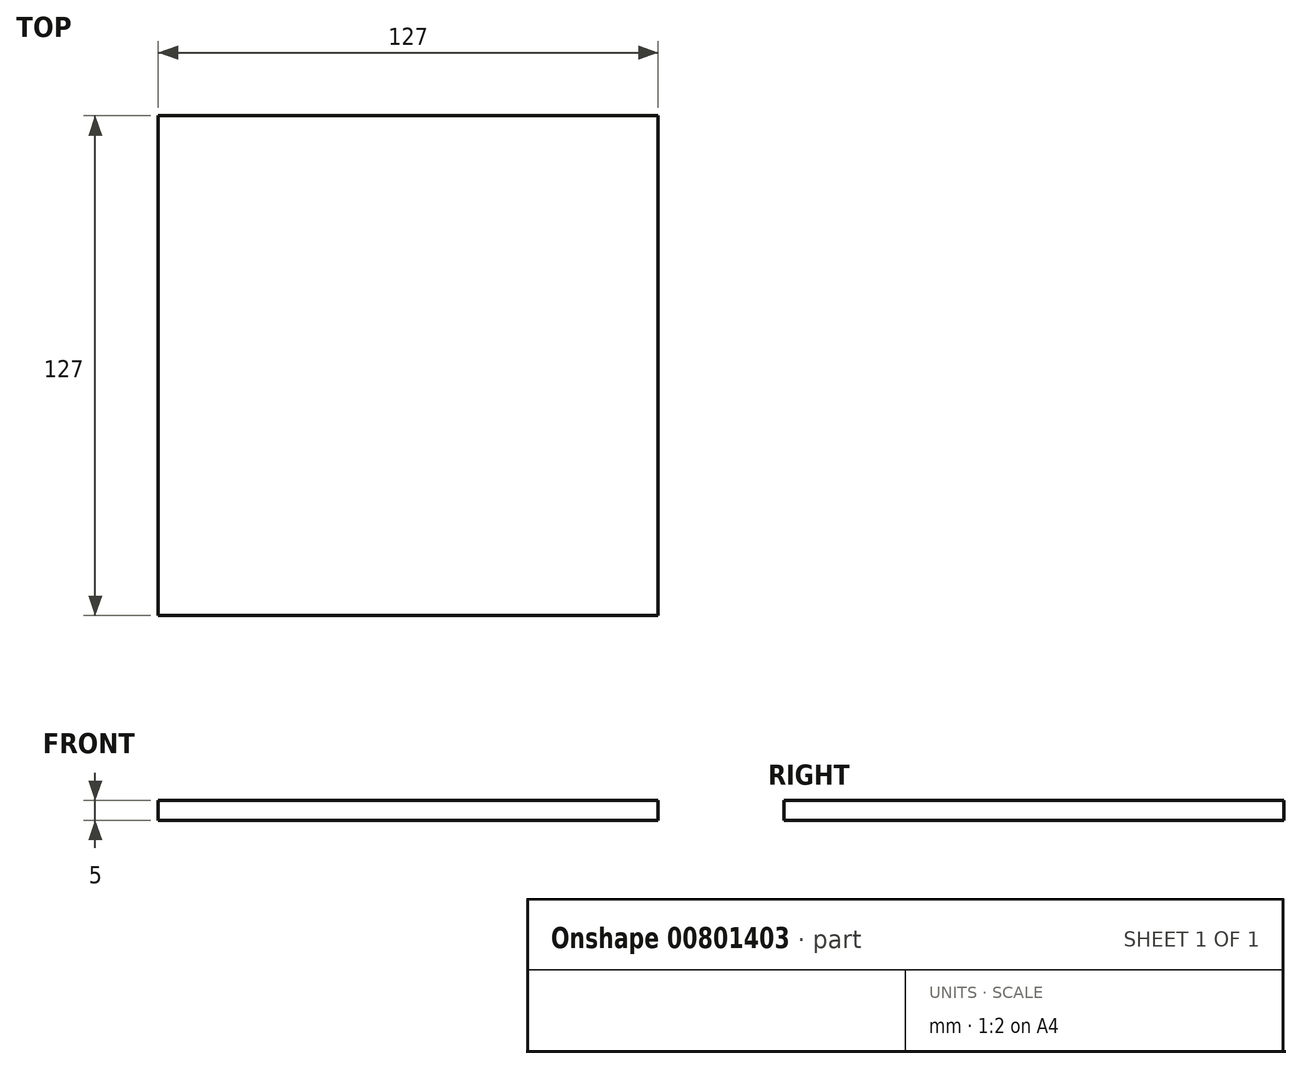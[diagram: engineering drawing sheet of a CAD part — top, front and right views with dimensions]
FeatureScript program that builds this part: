
annotation { "Feature Type Name" : "Feature", "Feature Type Description" : "" }
export const myFeature = defineFeature(function(context is Context, id is Id, definition is map)
    precondition{}
    {
        {
            var Q0;
            Q0=qCreatedBy(makeId("Top.planeOp"),FACE);
            var sketch = newSketch(context, id + "F0", { "sketchPlane" : qUnion([Q0])});
            skLineSegment(sketch, "E0.bottom", {"start": v(-63.5, 63.5) * mm, "end": v(63.5, 63.5) * mm});
            skLineSegment(sketch, "E0.top", {"start": v(-63.5, -63.5) * mm, "end": v(63.5, -63.5) * mm});
            skLineSegment(sketch, "E0.left", {"start": v(-63.5, 63.5) * mm, "end": v(-63.5, -63.5) * mm});
            skLineSegment(sketch, "E0.right", {"start": v(63.5, 63.5) * mm, "end": v(63.5, -63.5) * mm});
            skPoint(sketch, "E0.middle", {"position": v(0, 0) * mm});
            skSolve(sketch);
        }
        {
            var Q0;
            Q0 = qSketchRegion(id + "F0", true);
            extrude(context, id + "F1", {"entities" : qUnion([Q0]), "depth" : 5 * mm, "offsetDistance" : 25.4 * mm});
        }
    });
